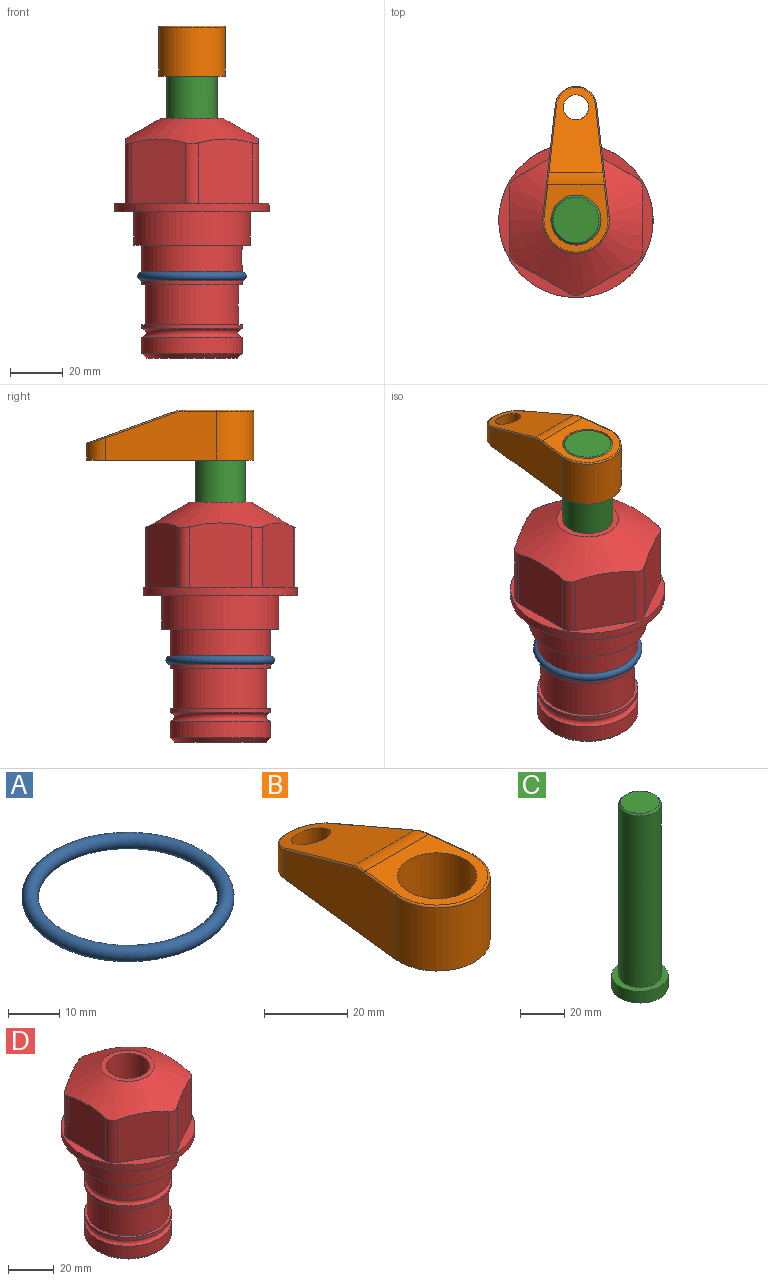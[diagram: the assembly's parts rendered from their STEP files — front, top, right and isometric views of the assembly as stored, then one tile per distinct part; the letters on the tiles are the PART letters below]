
ASSEMBLY  parts=4 mates=2
PART A: 1 faces, bbox 44.7x44.7x3.2 mm
  f0: torus R=19.05mm, axis (0,0,1), area 1193.9mm2
PART B: 44 faces, bbox 27.5x64.5x19.1 mm
  f0: plane 2.3x0.95mm, normal (0,0,-1), area 1mm2, adj f25,f30,f34
  f1: plane 63.5x25.4mm, normal (0,0,-1), area 561.7mm2, adj f2,f3,f4,f5,f6,f7,f19,f20
  f2: cylinder r=12.7mm len=25.4mm, axis (0,0,-1), area 792.2mm2, adj f1,f3,f5,f13
  f3: plane 42.33x18.54mm, normal (0.99,0.11,0), area 647mm2, adj f1,f2,f4,f11,f12,f14
  f4: cylinder r=7.94mm len=15.78mm, axis (0,0,-1), area 158.6mm2, adj f1,f3,f5,f16
  f5: plane 42.33x18.54mm, normal (-0.99,0.11,0), area 647mm2, adj f1,f2,f4,f15,f17,f18
  f6: cylinder r=9.53mm len=19.05mm, axis (0,0,-1), area 1140.1mm2, adj f1,f8
  f7: cylinder r=4.76mm len=10.98mm, axis (0,0,-1), area 276.1mm2, adj f1,f9
  f8: plane 25.83x24.38mm, normal (0,0,1), area 262.2mm2, adj f6,f10,f11,f13,f15
  f9: plane 32.49x20.55mm, normal (0,0.34,0.94), area 489.9mm2, adj f7,f10,f14,f16,f18
  f10: cylinder r=12.7mm len=21.49mm, axis (-1,0,0), area 93.2mm2, adj f8,f9,f12,f17
  f11: cylinder r=0.51mm len=12.34mm, axis (0.11,-0.99,0), area 9.9mm2, adj f3,f8,f12,f13
  f12: bspline ~7.62x1.64mm, area 3.5mm2, adj f3,f10,f11,f14
  f13: torus R=12.19mm, axis (0,0,1), area 33.6mm2, adj f2,f8,f11,f15
  f14: cylinder r=0.51mm len=26.01mm, axis (0.1,-0.93,0.34), area 21.6mm2, adj f3,f9,f12,f16
  f15: cylinder r=0.51mm len=12.34mm, axis (0.11,0.99,0), area 9.9mm2, adj f5,f8,f13,f17
  f16: bspline ~15.78x7.05mm, area 15.7mm2, adj f4,f9,f14,f18
  f17: bspline ~7.62x1.64mm, area 3.5mm2, adj f5,f10,f15,f18
  f18: cylinder r=0.51mm len=26.01mm, axis (0.1,0.93,-0.34), area 21.6mm2, adj f5,f9,f16,f17
  f19: plane 21.6x14.29mm, normal (-0.99,-0.11,0), area 242.6mm2, adj f1,f26,f28,f34,f36,f38
  f20: plane 21.6x14.29mm, normal (0.99,-0.11,0), area 242.6mm2, adj f1,f27,f29,f37,f39,f41
  f21: cylinder r=12.7mm len=14.29mm, axis (0,0,-1), area 173.2mm2, adj f1,f26,f27,f30,f31,f33
  f22: cylinder r=7.94mm len=7.63mm, axis (0,0,-1), area 53.8mm2, adj f1,f28,f29,f42
  f23: plane 2.3x0.95mm, normal (0,0,-1), area 1mm2, adj f25,f33,f37
  f24: plane 17.94x12.32mm, normal (0,-0.34,-0.94), area 191.2mm2, adj f25,f38,f41,f42
  f25: cylinder r=9.53mm len=12.93mm, axis (-1,0,0), area 37.5mm2, adj f0,f23,f24,f31,f36,f39
  f26: cylinder r=1.59mm len=14.29mm, axis (0,0,-1), area 49mm2, adj f1,f19,f21,f32
  f27: cylinder r=1.59mm len=14.29mm, axis (0,0,-1), area 49mm2, adj f1,f20,f21,f35
  f28: cylinder r=1.59mm len=7.28mm, axis (0,0,-1), area 22.1mm2, adj f1,f19,f22,f40
  f29: cylinder r=1.59mm len=7.28mm, axis (0,0,-1), area 22.1mm2, adj f1,f20,f22,f43
  f30: torus R=14.29mm, axis (0,0,1), area 5.8mm2, adj f0,f21,f31,f32
  f31: bspline ~11.06x2.73mm, area 20.8mm2, adj f21,f25,f30,f33
  f32: sphere r=1.59mm, area 5.4mm2, adj f26,f30,f34
  f33: torus R=14.29mm, axis (0,0,1), area 5.8mm2, adj f21,f23,f31,f35
  f34: cylinder r=1.59mm len=1.68mm, axis (-0.11,0.99,0), area 2.4mm2, adj f0,f19,f32,f36
  f35: sphere r=1.59mm, area 5.4mm2, adj f27,f33,f37
  f36: bspline ~5.82x2.33mm, area 7.7mm2, adj f19,f25,f34,f38
  f37: cylinder r=1.59mm len=1.68mm, axis (0.11,0.99,0), area 2.4mm2, adj f20,f23,f35,f39
  f38: cylinder r=1.59mm len=18.33mm, axis (0.1,-0.93,0.34), area 46.7mm2, adj f19,f24,f36,f40
  f39: bspline ~5.82x2.33mm, area 7.7mm2, adj f20,f25,f37,f41
  f40: sphere r=1.59mm, area 3.6mm2, adj f28,f38,f42
  f41: cylinder r=1.59mm len=18.33mm, axis (0.1,0.93,-0.34), area 46.7mm2, adj f20,f24,f39,f43
  f42: bspline ~8.31x1.84mm, area 15.3mm2, adj f22,f24,f40,f43
  f43: sphere r=1.59mm, area 3.6mm2, adj f29,f41,f42
PART C: 6 faces, bbox 25.4x25.4x101.6 mm
  f0: plane 17.46x17.46mm, normal (0,0,1), area 239.5mm2, adj f5
  f1: plane 25.4x25.4mm, normal (0,0,-1), area 506.7mm2, adj f2
  f2: cylinder r=12.7mm len=25.4mm, axis (0,0,1), area 506.7mm2, adj f1,f3
  f3: plane 25.4x25.4mm, normal (0,0,1), area 221.7mm2, adj f2,f4
  f4: cylinder r=9.53mm len=94.46mm, axis (0,0,1), area 5653mm2, adj f3,f5
  f5: cone r=8.73mm half-angle=45deg, axis (0,0,-1), area 64.4mm2, adj f0,f4
PART D: 36 faces, bbox 58.7x58.7x91.2 mm
  f0: cylinder r=17.78mm len=35.56mm, axis (0,0,1), area 1670.8mm2, adj f23,f24,f31
  f1: cylinder r=19.05mm len=38.1mm, axis (0,0,1), area 1191.9mm2, adj f26,f27,f30
  f2: plane 58.66x58.66mm, normal (0,0,-1), area 1150.6mm2, adj f3,f28
  f3: cylinder r=29.33mm len=58.66mm, axis (0,0,-1), area 585.1mm2, adj f2,f4
  f4: plane 58.66x58.66mm, normal (0,0,1), area 475.9mm2, adj f3,f5,f6,f7,f8,f9,f10,f11
  f5: plane 24.5x20.32mm, normal (-0.5,0.87,0), area 562.8mm2, adj f4,f15,f16,f17
  f6: plane 24.5x20.32mm, normal (0.5,0.87,0), area 562.8mm2, adj f4,f14,f15,f17
  f7: plane 24.5x23.48mm, normal (1,0,0), area 562.8mm2, adj f4,f13,f14,f17
  f8: plane 24.5x20.32mm, normal (0.5,-0.87,0), area 562.8mm2, adj f4,f12,f13,f17
  f9: plane 24.5x20.32mm, normal (-0.5,-0.87,0), area 562.8mm2, adj f4,f11,f12,f17
  f10: plane 24.5x23.48mm, normal (-1,0,0), area 562.8mm2, adj f4,f11,f16,f17
  f11: cylinder r=5.08mm len=23.01mm, axis (0,0,-1), area 121.2mm2, adj f4,f9,f10,f17
  f12: cylinder r=5.08mm len=23.01mm, axis (0,0,-1), area 121.2mm2, adj f4,f8,f9,f17
  f13: cylinder r=5.08mm len=23.01mm, axis (0,0,-1), area 121.2mm2, adj f4,f7,f8,f17
  f14: cylinder r=5.08mm len=23.01mm, axis (0,0,-1), area 121.2mm2, adj f4,f6,f7,f17
  f15: cylinder r=5.08mm len=23.01mm, axis (0,0,-1), area 121.2mm2, adj f4,f5,f6,f17
  f16: cylinder r=5.08mm len=23.01mm, axis (0,0,-1), area 121.2mm2, adj f4,f5,f10,f17
  f17: cone r=11.73mm half-angle=60deg, axis (0,0,-1), area 2071.8mm2, adj f5,f6,f7,f8,f9,f10,f11,f12
  f18: plane 23.46x23.46mm, normal (0,0,1), area 147.4mm2, adj f17,f35
  f19: plane 34.93x34.93mm, normal (0,0,-1), area 958mm2, adj f29
  f20: cylinder r=19.05mm len=38.1mm, axis (0,0,1), area 760.1mm2, adj f21,f29
  f21: torus R=19.05mm, axis (0,0,1), area 565.3mm2, adj f20,f22
  f22: cylinder r=19.05mm len=38.1mm, axis (0,0,1), area 190mm2, adj f21,f23
  f23: plane 38.1x38.1mm, normal (0,0,1), area 146.9mm2, adj f0,f22
  f24: plane 38.1x38.1mm, normal (0,0,-1), area 146.9mm2, adj f0,f25
  f25: cylinder r=19.05mm len=38.1mm, axis (0,0,1), area 190mm2, adj f24,f26
  f26: torus R=19.05mm, axis (0,0,1), area 565.3mm2, adj f1,f25
  f27: plane 44.45x44.45mm, normal (0,0,-1), area 411.7mm2, adj f1,f28
  f28: cylinder r=22.23mm len=44.45mm, axis (0,0,1), area 1773.5mm2, adj f2,f27
  f29: cone r=19.05mm half-angle=45deg, axis (0,0,1), area 257.5mm2, adj f19,f20
  f30: cylinder r=3.17mm len=6.75mm, axis (-1,0,0), area 128mm2, adj f1,f33
  f31: cylinder r=3.17mm len=6.35mm, axis (-1,0,0), area 102.5mm2, adj f0,f33
  f32: plane 25.4x25.4mm, normal (0,0,1), area 506.7mm2, adj f33
  f33: cylinder r=12.7mm len=66.42mm, axis (0,0,-1), area 5236.2mm2, adj f30,f31,f32,f34
  f34: cone r=9.53mm half-angle=30deg, axis (0,0,-1), area 443.4mm2, adj f33,f35
  f35: cylinder r=9.53mm len=19.05mm, axis (0,0,-1), area 849mm2, adj f18,f34
PLACE A at identity
PLACE B t=(0,0,51.56)mm
PLACE C t=(0,0,-3.05)mm
PLACE D at identity fixed
MATE cylindrical C.f2 <-> D.f0  axis (0,0,1) through (0,0,22.59)mm
MATE fastened B.f2 <-> C.f2  axis (0,0,-1) through (0,0,70.61)mm
